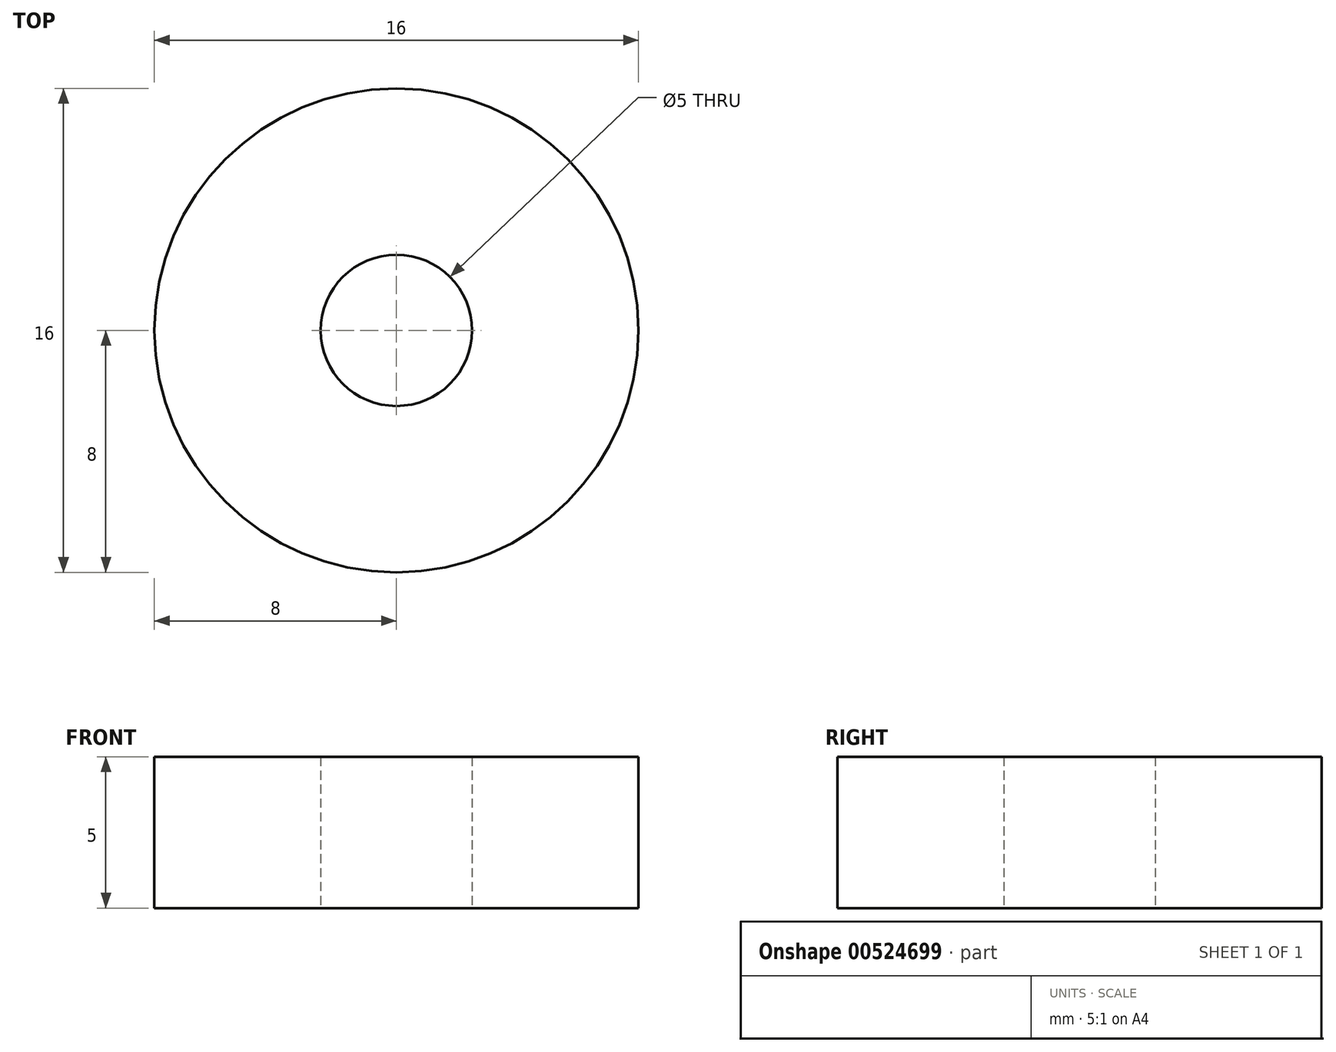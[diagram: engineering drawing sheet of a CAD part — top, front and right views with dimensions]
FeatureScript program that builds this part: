
annotation { "Feature Type Name" : "Feature", "Feature Type Description" : "" }
export const myFeature = defineFeature(function(context is Context, id is Id, definition is map)
    precondition{}
    {
        {
            var Q0;
            Q0=qCreatedBy(makeId("Top.planeOp"),FACE);
            var sketch = newSketch(context, id + "F0", { "sketchPlane" : qUnion([Q0])});
            skCircle(sketch, "E0", {"center": v(0, 0) * mm, "radius": 2.5 * mm});
            skCircle(sketch, "E1", {"center": v(0, 0) * mm, "radius": 8 * mm});
            skSolve(sketch);
        }
        {
            var Q0;
            Q0=makeQuery(id+"F0.imprint","IMPRINT",FACE,{"disambiguationData":[TD([[makeQuery(id+"F0.imprint","IMPRINT",EDGE,{"derivedFrom":sQuery(id+"F0.wireOp",EDGE,"E0")}),-1.0]])]});
            extrude(context, id + "F1", {"entities" : qUnion([Q0]), "depth" : 5 * mm, "offsetDistance" : 25 * mm});
        }
    });
